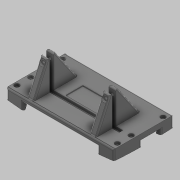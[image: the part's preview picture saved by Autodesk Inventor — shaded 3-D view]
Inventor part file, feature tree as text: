
AUTODESK INVENTOR PART (.ipt)
format: ipt  version: 2020 (Build 240168000, 168)  size: 7,907,840 bytes
history: native  units: in
note: dims shown in document units (in); Inventor stores cm internally (conversion verified against a paired STEP export)
features: sketch x16, extrude x12, plane x8, chamfer x7, other x6, fillet x4, revolve x3, split x3, hole x3, projected_geometry x2, sweep x1
ambient origin geometry x8: Origin, YZ Plane, XZ Plane, XY Plane, X Axis, Y Axis, Z Axis, Center Point
bodies: Solid7 (feature_tree), Solid8 (feature_tree), Solid10 (feature_tree)
feature tree (65):
  other  "ProfileTop"
  other  "ProfileSide"
  other  "XY_Project"
  other  "ProfileBack"
  revolve  "RevolvePlane"  [1 undecoded]
  revolve  "RevolveSketch"  [1 undecoded]
  extrude  "Extrusion5"  Depth=7.874in
  extrude  "Extrusion6"  Depth=5.4528in
  split  "Split1"
  revolve  "Revolution1"  [1 undecoded]
  chamfer  "Chamfer4"  Distance=1.8083in
  chamfer  "Chamfer5"  Distance=1.6341in
  chamfer  "Chamfer6"  Distance=0.8398in
  chamfer  "Chamfer7"  [1 undecoded]
  sweep  "Sweep1"
  chamfer  "Chamfer8"  Distance=0.1969in
  chamfer  "Chamfer9"  Distance=0.1969in
  chamfer  "Chamfer10"  Distance=29.8893in
  other  "SensorDivet"
  extrude  "Extrusion7"  Depth=0.0984in
  plane  "Work Plane6"
  plane  "Work Plane8"
  sketch  "Sketch12"  dims[d112=30.973in d142=7.874in]
  extrude  "BackSupport"  Depth=0.0984in
  extrude  "FrontSupport"  Depth=0.0984in
  plane  "Work Plane9"
  sketch  "Sketch19"  dims[d159=2.937in d160=16.7023in]
  sketch  "Sketch21"  dims[d161=16.7023in]
  extrude  "BaseVerticalExtend"  Depth=0.0984in
  plane  "Work Plane10"
  extrude  "BasePlate"  Depth=0.0984in
  extrude  "TriRib"  Depth=0.0984in
  extrude  "Slot"  Depth=0.0984in
  plane  "Work Plane11"
  extrude  "Extrusion19"  Depth=0.0984in
  extrude  "Extrusion20"  Depth=0.0984in TaperAngle=0.0deg
  hole  "Hole2"  [1 undecoded]
  fillet  "Fillet1"  [1 undecoded]
  fillet  "Fillet2"  Radius=1.4961in
  fillet  "Fillet3"  Radius=1.4961in
  plane  "Work Plane13"
  split  "Split7"
  split  "Split8"
  plane  "Work Plane15"
  hole  "Hole3"  [1 undecoded]
  plane  "Work Plane16"
  hole  "Hole4"  [1 undecoded]
  extrude  "Extrusion21"  Depth=0.0984in TaperAngle=45.0deg
  fillet  "Fillet4"  Radius=0.1969in
  other  "Image8"
  sketch  "Sketch9"  dims[d98=7.874in d109=2.278in]
  sketch  "3D Sketch1"
  sketch  "Sketch10"  dims[d110=12.4228in d111=3.715in]
  sketch  "Sketch13"  dims[d155=5.4528in d158=5.4528in]
  projected_geometry  "Projected Loop1"
  projected_geometry  "Projected Loop2"
  sketch  "Sketch22"  dims[d162=2.937in]
  sketch  "Sketch23"  dims[d170=1.8504in]
  sketch  "Sketch24"  dims[d171=7.4452in]
  sketch  "Sketch26"  dims[d172=5.4724in]
  sketch  "Sketch27"  dims[d173=0.0in]
  sketch  "Sketch29"  dims[d174=4.9332in]
  sketch  "Sketch32"  dims[d175=5.4231in]
  sketch  "Sketch33"  dims[d176=1.7487in]
  sketch  "Sketch34"  dims[d177=4.8557in d178=1.8083in d179=1.6341in d180=0.8398in d181=0.0in d187=0.5906in d188=0.1969in d189=0.1969in d272=29.8893in d278=8.1496in d279=1.2598in d280=10.9449in d281=6.8898in d282=1.2598in d283=5.4724in d284=5.4724in d285=8.1496in d288=15.748in d289=0.0in d290=15.748in d291=0.0in d346=180.0deg d347=1.4961in d348=1.4961in d349=5.4724in d350=0.1969in d351=1.4961in d352=45.0deg d353=0.1969in d354=1.4961in d355=45.0deg d356=0.1969in d357=1.4961in d358=45.0deg d359=0.1969in d360=1.4961in d361=45.0deg d362=0.0in d363=0.0in d364=0.1969in d365=1.4961in d366=45.0deg d367=0.1969in d368=1.4961in d369=45.0deg d370=0.0591in d371=1.4961in d372=45.0deg d373=-1.9685in d375=0.0in d376=0.0in d377=1.4961in d378=1.4961in d379=0.0in d380=0.6693in d381=0.6693in d382=0.6693in d383=0.6693in d384=0.6693in d385=0.6693in d386=0.5512in d387=0.9055in d388=0.0in d397=-1.9685in d424=0.3937in d425=0.0in d426=1.9685in d427=0.0in d428=12.2047in d429=3.1496in d430=6.1024in d431=0.5906in d432=12.2047in d433=6.1024in d434=1.5748in d457=0.3937in d458=0.0in d459=0.0in d460=0.5906in d461=0.0in d462=3.1496in d463=3.1496in d464=0.7874in d465=0.7874in d466=4.9213in d467=4.9213in d468=0.1969in d469=0.1969in d470=3.937in d471=0.0in d479=0.4134in d480=0.7972in d481=0.0in d482=4.2126in d483=4.2126in d484=8.6713in d485=0.0in d490=-2.3622in d491=0.7874in d492=0.7874in d493=1.1811in d494=0.0in d495=0.7874in d496=0.7874in d497=0.7874in d498=0.0in d512=0.3937in d513=0.3937in d514=0.3937in d515=0.3937in d516=0.7874in d517=0.7874in d518=0.7874in d519=0.7874in d520=0.3937in d521=0.3937in d522=0.7874in d523=0.7874in d524=0.3346in d525=0.2362in d526=0.5512in d527=0.2756in d528=90.0deg d529=2.3622in d530=0.8108in d532=0.1969in d533=0.1575in d534=0.1575in d535=1.1811in d541=1.3061in d542=3.2283in d543=3.2283in d544=0.3346in d545=0.2362in d546=0.5512in d547=0.2756in d548=90.0deg d549=2.3622in d550=0.8108in d551=0.3937in d552=0.3937in d553=0.9936in d554=3.2283in d555=3.2283in d556=0.3937in d557=0.3937in d558=0.3346in d559=0.2362in d560=0.6299in d561=0.2756in d562=90.0deg d563=2.3622in d564=0.8108in d565=1.9685in d566=0.1969in d567=1.9685in d568=3.937in d571=1.1811in d572=0.0984in d573=0.0in d574=0.0984in d163=0.0197in d164=0.0344in d165=0.0197in d166=0.0344in d440=0.0197in d441=0.0344in d442=0.0197in d443=0.0344in d449=0.0197in d450=0.0344in d451=0.0197in d452=0.0344in d540=0.0394in]
note: 8 required parameter values undecoded (feature->parameter linkage not recoverable at this tier; creation-order binding heuristic only, values carry confidence <= 0.55)